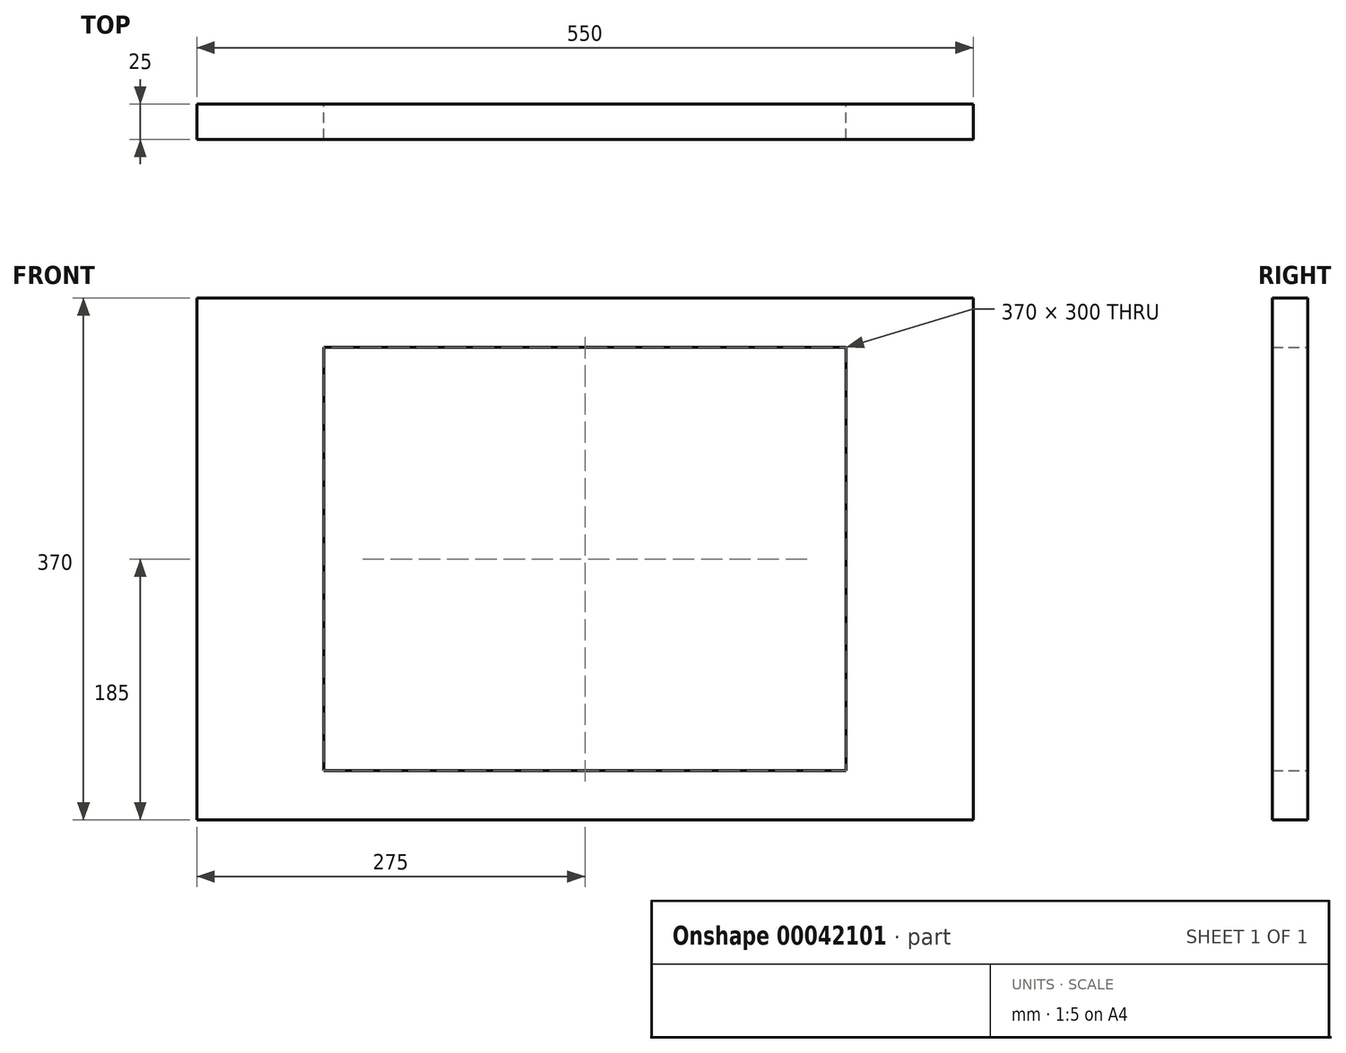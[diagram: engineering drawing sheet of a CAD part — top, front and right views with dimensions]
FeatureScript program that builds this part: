
annotation { "Feature Type Name" : "Feature", "Feature Type Description" : "" }
export const myFeature = defineFeature(function(context is Context, id is Id, definition is map)
    precondition{}
    {
        {
            var Q0;
            Q0=qCreatedBy(makeId("Front.planeOp"),FACE);
            var sketch = newSketch(context, id + "F0", { "sketchPlane" : qUnion([Q0])});
            skLineSegment(sketch, "E0.rect.bottom", {"start": v(275, -185) * mm, "end": v(-275, -185) * mm});
            skLineSegment(sketch, "E0.rect.top", {"start": v(275, 185) * mm, "end": v(-275, 185) * mm});
            skLineSegment(sketch, "E0.rect.left", {"start": v(275, -185) * mm, "end": v(275, 185) * mm});
            skLineSegment(sketch, "E0.rect.right", {"start": v(-275, -185) * mm, "end": v(-275, 185) * mm});
            skPoint(sketch, "E0.rect.middle", {"position": v(0, 0) * mm});
            skLineSegment(sketch, "E1.rect.bottom", {"start": v(185, -150) * mm, "end": v(-185, -150) * mm});
            skLineSegment(sketch, "E1.rect.top", {"start": v(185, 150) * mm, "end": v(-185, 150) * mm});
            skLineSegment(sketch, "E1.rect.left", {"start": v(185, -150) * mm, "end": v(185, 150) * mm});
            skLineSegment(sketch, "E1.rect.right", {"start": v(-185, -150) * mm, "end": v(-185, 150) * mm});
            skSolve(sketch);
        }
        {
            var Q0;
            Q0 = qSketchRegion(id + "F0", true);
            extrude(context, id + "F1", {"entities" : qUnion([Q0]), "depth" : 25 * mm});
        }
    });
